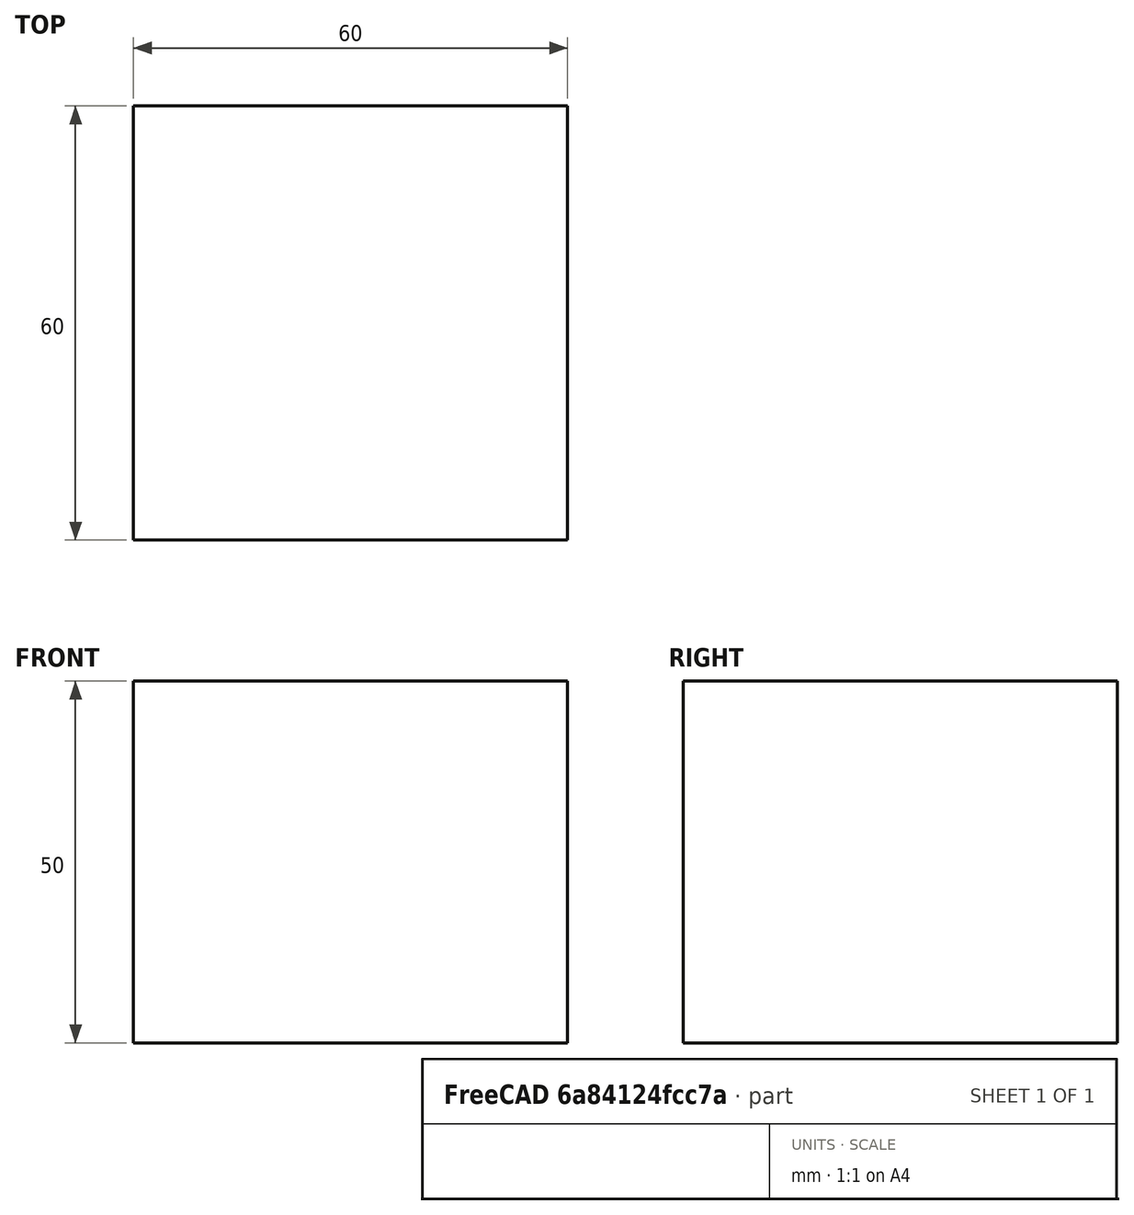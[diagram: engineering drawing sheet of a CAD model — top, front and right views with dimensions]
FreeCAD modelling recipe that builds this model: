
FCSTD DOCUMENT  (FreeCAD 0.15R4671 (Git))
Label: Square Bar 60 EN10059 S235JR
License: All rights reserved
LicenseURL: http://en.wikipedia.org/wiki/All_rights_reserved
objects: Sketcher::SketchObject×1, Part::Extrusion×1
note: 2 computed .brp shape members not serialized (recipe doc carries the construction recipe); baked Part::Feature solids carry a one-line shape summary decoded from their .brp

FEATURE [Sketcher::SketchObject] Sketch
  sketch-geometry (4):
    g0: LineSegment StartX=-30 StartY=-30 StartZ=0 EndX=30 EndY=-30 EndZ=0
    g1: LineSegment StartX=30 StartY=-30 StartZ=0 EndX=30 EndY=30 EndZ=0
    g2: LineSegment StartX=30 StartY=30 StartZ=0 EndX=-30 EndY=30 EndZ=0
    g3: LineSegment StartX=-30 StartY=30 StartZ=0 EndX=-30 EndY=-30 EndZ=0
  constraints (12):
    c: Coincident(g0,g1)
    c: Coincident(g1,g2)
    c: Coincident(g2,g3)
    c: Coincident(g3,g0)
    c: Horizontal(g0)
    c: Horizontal(g2)
    c: Vertical(g1)
    c: Vertical(g3)
    c: Symmetric(g1,g0,g-1)
    c: Symmetric(g2,g1,g-2)
    c: Equal(g1,g2)
    c: DistanceY(g1) = 60
FEATURE [Part::Extrusion] Extrude  label="Square Bar 60 EN10059 S235JR"
  Base = -> Sketch
  Dir = (0,0,50)
  Solid = true
